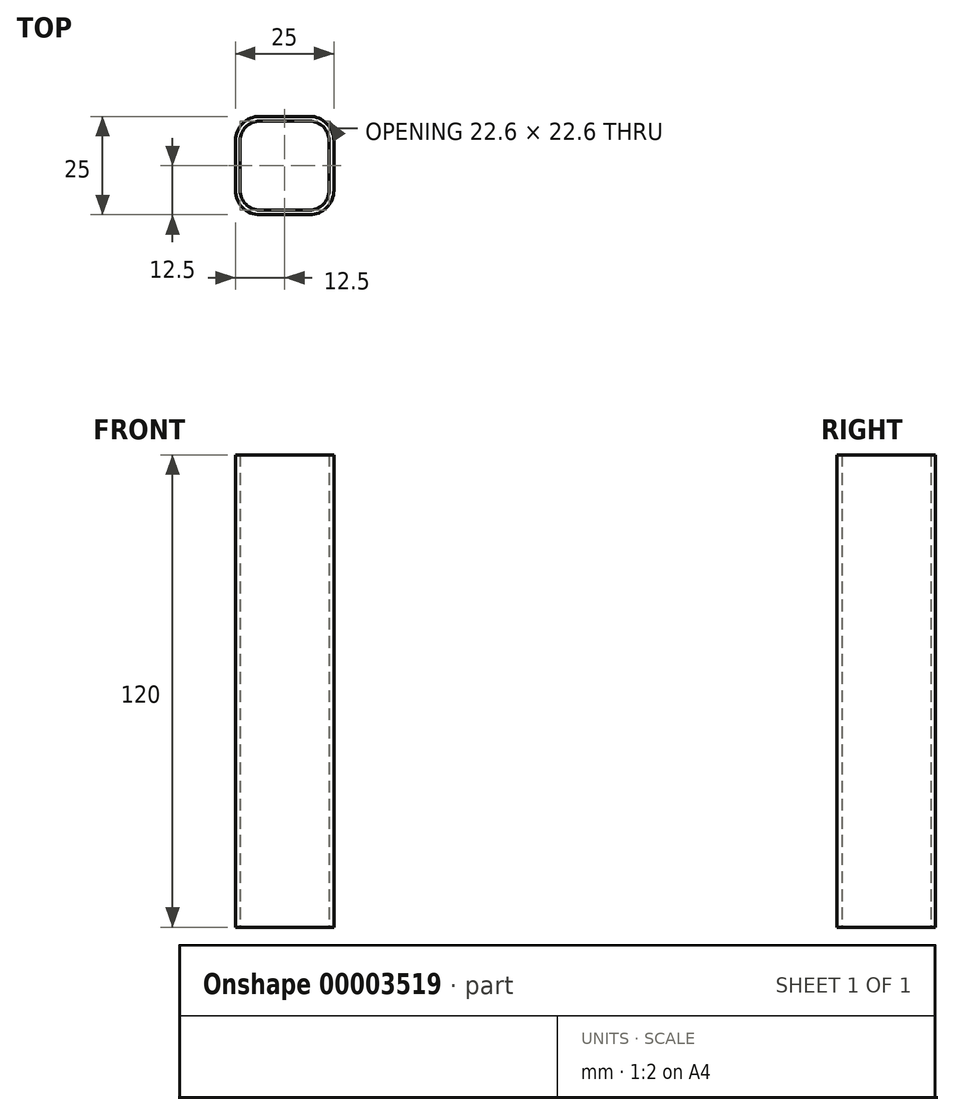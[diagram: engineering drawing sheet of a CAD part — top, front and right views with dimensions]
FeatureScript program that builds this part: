
annotation { "Feature Type Name" : "Feature", "Feature Type Description" : "" }
export const myFeature = defineFeature(function(context is Context, id is Id, definition is map)
    precondition{}
    {
        {
            var Q0;
            Q0=qCreatedBy(makeId("Top.planeOp"),FACE);
            var sketch = newSketch(context, id + "F0", { "sketchPlane" : qUnion([Q0])});
            skLineSegment(sketch, "E0.rect.bottom", {"start": v(6.3, -12.5) * mm, "end": v(-6.3, -12.5) * mm});
            skLineSegment(sketch, "E0.rect.top", {"start": v(6.3, 12.5) * mm, "end": v(-6.3, 12.5) * mm});
            skLineSegment(sketch, "E0.rect.left", {"start": v(12.5, -6.3) * mm, "end": v(12.5, 6.3) * mm});
            skLineSegment(sketch, "E0.rect.right", {"start": v(-12.5, -6.3) * mm, "end": v(-12.5, 6.3) * mm});
            skPoint(sketch, "E0.rect.middle", {"position": v(0, 0) * mm});
            skLineSegment(sketch, "E1.rect.bottom", {"start": v(6.3, -11.3) * mm, "end": v(-6.3, -11.3) * mm});
            skLineSegment(sketch, "E1.rect.top", {"start": v(6.3, 11.3) * mm, "end": v(-6.3, 11.3) * mm});
            skLineSegment(sketch, "E1.rect.left", {"start": v(11.3, -6.3) * mm, "end": v(11.3, 6.3) * mm});
            skLineSegment(sketch, "E1.rect.right", {"start": v(-11.3, -6.3) * mm, "end": v(-11.3, 6.3) * mm});
            skPoint(sketch, "E2.visualSharp", {"position": v(-11.3, 11.3) * mm});
            skArc(sketch, "E2.filletArc", {"start": v(-6.3, 11.3) * mm, "mid": v(-9.84, 9.84) * mm, "end": v(-11.3, 6.3) * mm});
            skPoint(sketch, "E3.visualSharp", {"position": v(-11.3, -11.3) * mm});
            skArc(sketch, "E3.filletArc", {"start": v(-11.3, -6.3) * mm, "mid": v(-9.84, -9.84) * mm, "end": v(-6.3, -11.3) * mm});
            skPoint(sketch, "E4.visualSharp", {"position": v(11.3, 11.3) * mm});
            skArc(sketch, "E4.filletArc", {"start": v(11.3, 6.3) * mm, "mid": v(9.84, 9.84) * mm, "end": v(6.3, 11.3) * mm});
            skPoint(sketch, "E5.visualSharp", {"position": v(11.3, -11.3) * mm});
            skArc(sketch, "E5.filletArc", {"start": v(6.3, -11.3) * mm, "mid": v(9.84, -9.84) * mm, "end": v(11.3, -6.3) * mm});
            skPoint(sketch, "E6.visualSharp", {"position": v(-12.5, -12.5) * mm});
            skArc(sketch, "E6.filletArc", {"start": v(-12.5, -6.3) * mm, "mid": v(-10.68, -10.68) * mm, "end": v(-6.3, -12.5) * mm});
            skPoint(sketch, "E7.visualSharp", {"position": v(-12.5, 12.5) * mm});
            skArc(sketch, "E7.filletArc", {"start": v(-6.3, 12.5) * mm, "mid": v(-10.68, 10.68) * mm, "end": v(-12.5, 6.3) * mm});
            skPoint(sketch, "E8.visualSharp", {"position": v(12.5, 12.5) * mm});
            skArc(sketch, "E8.filletArc", {"start": v(12.5, 6.3) * mm, "mid": v(10.68, 10.68) * mm, "end": v(6.3, 12.5) * mm});
            skPoint(sketch, "E9.visualSharp", {"position": v(12.5, -12.5) * mm});
            skArc(sketch, "E9.filletArc", {"start": v(6.3, -12.5) * mm, "mid": v(10.68, -10.68) * mm, "end": v(12.5, -6.3) * mm});
            skSolve(sketch);
        }
        {
            var Q0;
            Q0 = qSketchRegion(id + "F0", true);
            extrude(context, id + "F1", {"entities" : qUnion([Q0]), "depth" : 120 * mm});
        }
    });
